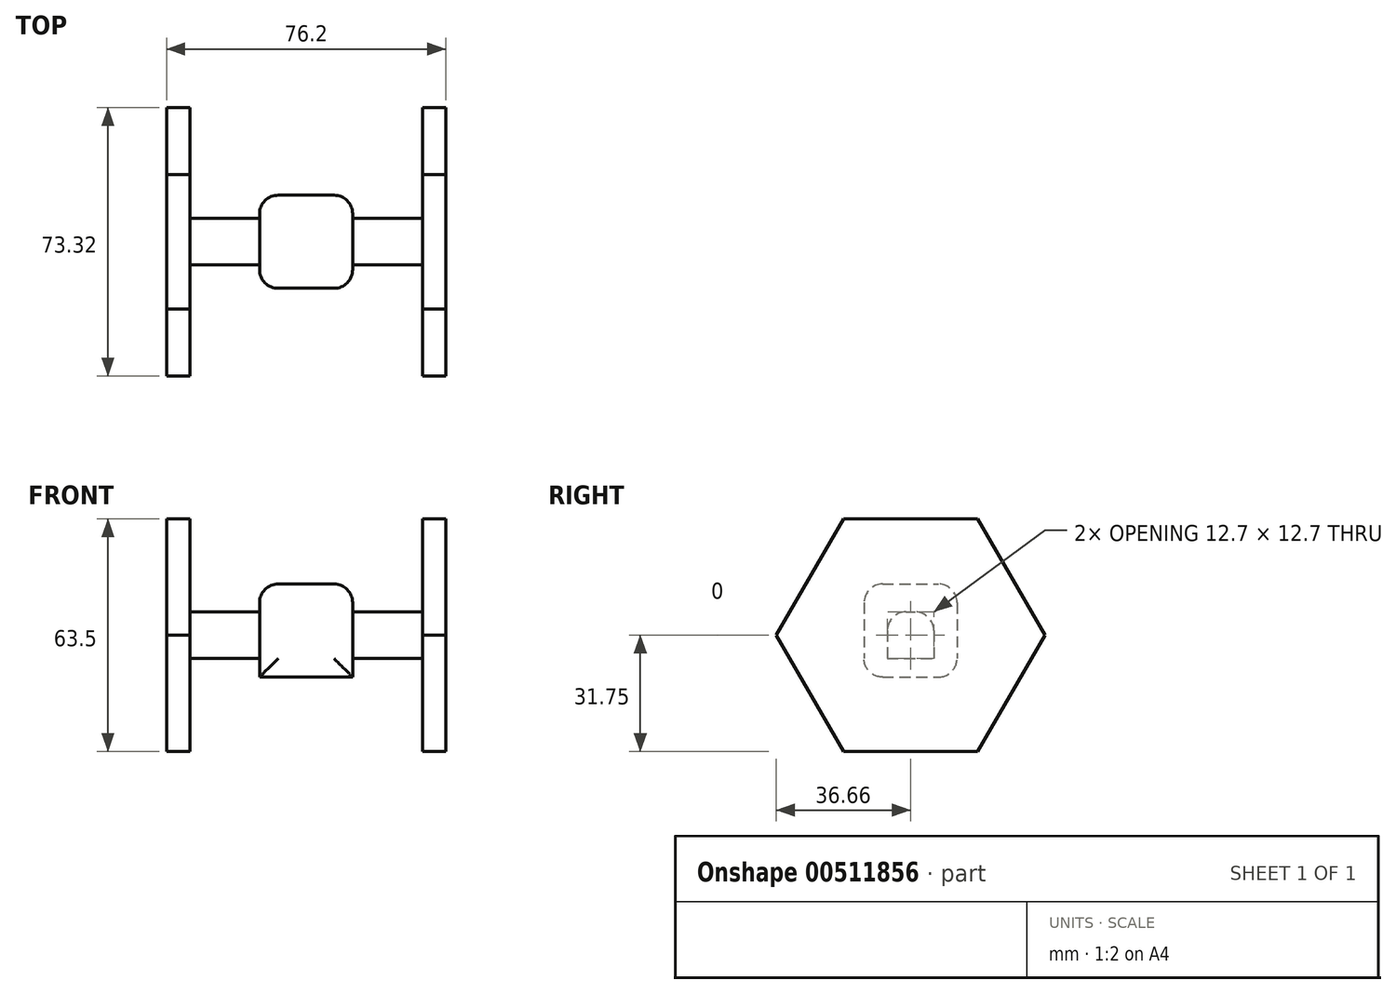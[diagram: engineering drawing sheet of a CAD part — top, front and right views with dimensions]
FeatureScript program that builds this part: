
annotation { "Feature Type Name" : "Feature", "Feature Type Description" : "" }
export const myFeature = defineFeature(function(context is Context, id is Id, definition is map)
    precondition{}
    {
        {
            var Q0;
            Q0=qCreatedBy(makeId("Right.planeOp"),FACE);
            var sketch = newSketch(context, id + "F0", { "sketchPlane" : qUnion([Q0])});
            skLineSegment(sketch, "E0.bottom", {"start": v(-6.35, 6.35) * mm, "end": v(6.35, 6.35) * mm});
            skLineSegment(sketch, "E0.top", {"start": v(-6.35, -6.35) * mm, "end": v(6.35, -6.35) * mm});
            skLineSegment(sketch, "E0.left", {"start": v(-6.35, 6.35) * mm, "end": v(-6.35, -6.35) * mm});
            skLineSegment(sketch, "E0.right", {"start": v(6.35, 6.35) * mm, "end": v(6.35, -6.35) * mm});
            skSolve(sketch);
        }
        {
            var Q0;
            Q0 = qSketchRegion(id + "F0", true);
            extrude(context, id + "F1", {"entities" : qUnion([Q0]), "depth" : 38.1 * mm});
        }
        {
            var Q0;
            {var subQ0=makeQuery(id+"F1.opExtrude","SWEPT_FACE",FACE,{"disambiguationData":[OSD([sQuery(id+"F0.wireOp",EDGE,"E0.bottom")])]});Q0=makeQuery(id+"FX4o8xcdrBZzJYz_1.boolean.opBoolean","MERGE",FACE,{"derivedFrom":[subQ0,makeQuery(id+"FX4o8xcdrBZzJYz_1.opPattern","COPY",FACE,{"derivedFrom":subQ0,"instanceName":"1"})]});}
            fillet(context, id + "F2", {"entities" : qUnion([Q0]), "radius" : 5.08 * mm, "tangentPropagation" : true, "allowEdgeOverflow" : false});
        }
        {
            var Q0;
            Q0=qCreatedBy(makeId("Right.planeOp"),FACE);
            var sketch = newSketch(context, id + "F3", { "sketchPlane" : qUnion([Q0])});
            skLineSegment(sketch, "E1.bottom", {"start": v(-12.7, 13.97) * mm, "end": v(12.7, 13.97) * mm});
            skLineSegment(sketch, "E1.top", {"start": v(-12.7, -11.43) * mm, "end": v(12.7, -11.43) * mm});
            skLineSegment(sketch, "E1.left", {"start": v(-12.7, 13.97) * mm, "end": v(-12.7, -11.43) * mm});
            skLineSegment(sketch, "E1.right", {"start": v(12.7, 13.97) * mm, "end": v(12.7, -11.43) * mm});
            skSolve(sketch);
        }
        {
            var Q0;
            Q0 = qSketchRegion(id + "F3", true);
            extrude(context, id + "F4", {"entities" : qUnion([Q0]), "operationType" : NewBodyOperationType.ADD, "depth" : 12.7 * mm});
        }
        {
            var Q0;
            Q0=makeQuery(id+"F1.opExtrude","CAP_FACE",FACE,{"disambiguationData":[OSD([sQuery(id+"F0.wireOp",EDGE,"E0.bottom"),sQuery(id+"F0.wireOp",EDGE,"E0.top"),sQuery(id+"F0.wireOp",EDGE,"E0.left"),sQuery(id+"F0.wireOp",EDGE,"E0.right")])],"isStart":false});
            var sketch = newSketch(context, id + "F5", { "sketchPlane" : qUnion([Q0])});
            skCircle(sketch, "E2.cCircle", {"center": v(0, 0) * mm, "radius": 31.75 * mm, "construction": true});
            skLineSegment(sketch, "E2.0", {"start": v(18.33, -31.75) * mm, "end": v(-18.33, -31.75) * mm});
            skLineSegment(sketch, "E2.1", {"start": v(-18.33, -31.75) * mm, "end": v(-36.66, 0) * mm});
            skLineSegment(sketch, "E2.2", {"start": v(-36.66, 0) * mm, "end": v(-18.33, 31.75) * mm});
            skLineSegment(sketch, "E2.3", {"start": v(-18.33, 31.75) * mm, "end": v(18.33, 31.75) * mm});
            skLineSegment(sketch, "E2.4", {"start": v(18.33, 31.75) * mm, "end": v(36.66, 0) * mm});
            skLineSegment(sketch, "E2.5", {"start": v(36.66, 0) * mm, "end": v(18.33, -31.75) * mm});
            skPoint(sketch, "E2.0.midPoint", {"position": v(0, -31.75) * mm});
            skSolve(sketch);
        }
        {
            var Q0;
            Q0 = qSketchRegion(id + "F5", true);
            extrude(context, id + "F6", {"entities" : qUnion([Q0]), "operationType" : NewBodyOperationType.ADD, "depth" : -6.35 * mm});
        }
        {
            var Q0;
            Q0=makeQuery(id+"F1.opExtrude","SWEPT_BODY",BODY,{"disambiguationData":[OSD([sQuery(id+"F0.wireOp",EDGE,"E0.bottom"),sQuery(id+"F0.wireOp",EDGE,"E0.top"),sQuery(id+"F0.wireOp",EDGE,"E0.left"),sQuery(id+"F0.wireOp",EDGE,"E0.right")])]});
            var Q1;
            Q1=qCreatedBy(makeId("Right.planeOp"),FACE);
            mirror(context, id + "F7", {"operationType" : NewBodyOperationType.ADD, "entities" : qUnion([Q0]), "mirrorPlane" : qUnion([Q1])});
        }
        {
            var Q0;
            {var subQ0=makeQuery(id+"F4.opExtrude","SWEPT_FACE",FACE,{"disambiguationData":[OSD([sQuery(id+"F3.wireOp",EDGE,"E1.bottom")])]});Q0=makeQuery(id+"F7.boolean.opBoolean","MERGE",FACE,{"derivedFrom":[subQ0,makeQuery(id+"F7.opPattern","COPY",FACE,{"derivedFrom":subQ0,"instanceName":"1"})]});}
            fillet(context, id + "F8", {"entities" : qUnion([Q0]), "radius" : 5.08 * mm, "tangentPropagation" : true, "allowEdgeOverflow" : false});
        }
        {
            var Q0;
            {var subQ0=makeQuery(id+"F4.opExtrude","SWEPT_FACE",FACE,{"disambiguationData":[OSD([sQuery(id+"F3.wireOp",EDGE,"E1.left")])]});Q0=makeQuery(id+"F7.boolean.opBoolean","MERGE",FACE,{"derivedFrom":[subQ0,makeQuery(id+"F7.opPattern","COPY",FACE,{"derivedFrom":subQ0,"instanceName":"1"})]});}
            fillet(context, id + "F9", {"entities" : qUnion([Q0]), "radius" : 5.08 * mm, "tangentPropagation" : true, "allowEdgeOverflow" : false});
        }
        {
            var Q0;
            {var subQ0=makeQuery(id+"F4.opExtrude","SWEPT_FACE",FACE,{"disambiguationData":[OSD([sQuery(id+"F3.wireOp",EDGE,"E1.right")])]});Q0=makeQuery(id+"F7.boolean.opBoolean","MERGE",FACE,{"derivedFrom":[subQ0,makeQuery(id+"F7.opPattern","COPY",FACE,{"derivedFrom":subQ0,"instanceName":"1"})]});}
            fillet(context, id + "F10", {"entities" : qUnion([Q0]), "radius" : 5.08 * mm, "tangentPropagation" : true, "allowEdgeOverflow" : false});
        }
    });
